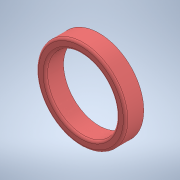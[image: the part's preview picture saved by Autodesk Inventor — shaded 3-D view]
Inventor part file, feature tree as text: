
AUTODESK INVENTOR PART (.ipt)
format: ipt  version: 2020.1 (Build 241239000, 239)  size: 173,056 bytes
history: native  units: in
note: dims shown in document units (in); Inventor stores cm internally (conversion verified against a paired STEP export)
features: other x1, extrude x1, fillet x1, sketch x1
ambient origin geometry x8: Origin, YZ Plane, XZ Plane, XY Plane, X Axis, Y Axis, Z Axis, Center Point
bodies: Solid1 (feature_tree)
feature tree (4):
  parser-record x1  (decoder bookkeeping rows leaked as tree rows — omitted from the tree; the rows remain in map.json)
  extrude  "Extrusion1"  Depth=0.0098in
  fillet  "Fillet1"  Radius=0.0787in
  sketch  "Sketch1"  dims[d0=0.3071in d1=0.0394in d2=0.0787in d3=0.0in d4=0.0098in]
note: 1 file-system path scrubbed to <path> (originals preserved in map.json)
